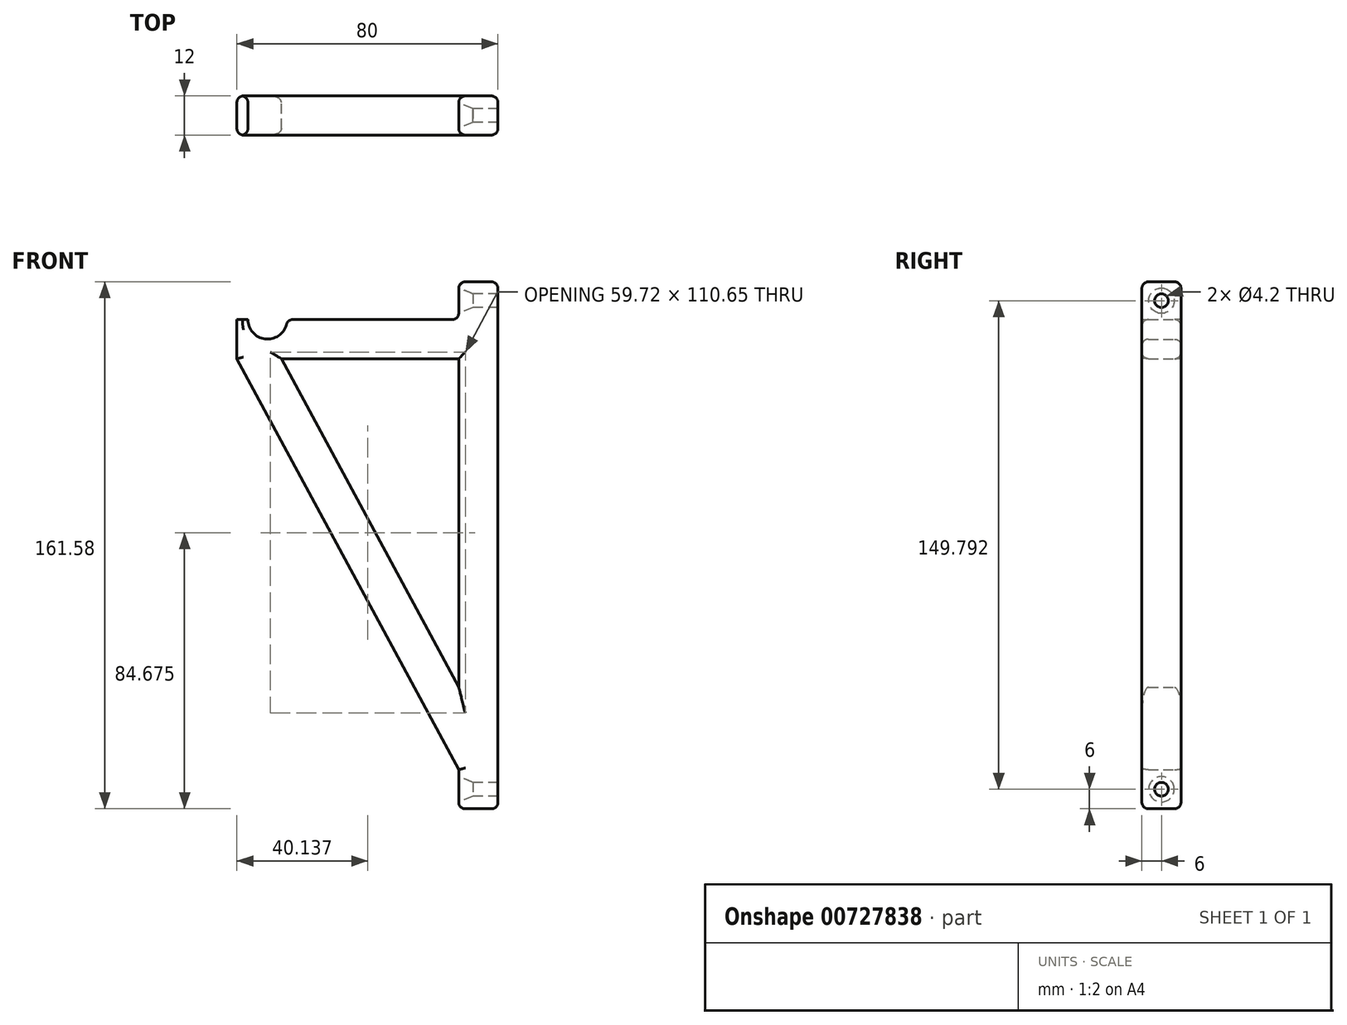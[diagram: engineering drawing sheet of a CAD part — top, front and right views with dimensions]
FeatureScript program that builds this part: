
annotation { "Feature Type Name" : "Feature", "Feature Type Description" : "" }
export const myFeature = defineFeature(function(context is Context, id is Id, definition is map)
    precondition{}
    {
        {
            var Q0;
            Q0=qCreatedBy(makeId("Front.planeOp"),FACE);
            var sketch = newSketch(context, id + "F0", { "sketchPlane" : qUnion([Q0])});
            skLineSegment(sketch, "E0", {"start": v(-21.3, 0) * mm, "end": v(46.7, 0) * mm});
            skLineSegment(sketch, "E1", {"start": v(46.7, 0) * mm, "end": v(46.7, -138) * mm});
            skLineSegment(sketch, "E2", {"start": v(46.7, -138) * mm, "end": v(58.7, -138) * mm});
            skLineSegment(sketch, "E3", {"start": v(58.7, -138) * mm, "end": v(58.7, -26.14) * mm});
            skLineSegment(sketch, "E4", {"start": v(58.7, -26.14) * mm, "end": v(58.7, 12) * mm});
            skLineSegment(sketch, "E5", {"start": v(58.7, 12) * mm, "end": v(-5.93, 12) * mm});
            skLineSegment(sketch, "E6", {"start": v(-21.3, 12) * mm, "end": v(-21.3, 0) * mm});
            skArc(sketch, "E7", {"start": v(-17.93, 12) * mm, "mid": v(-11.93, 6) * mm, "end": v(-5.93, 12) * mm});
            skLineSegment(sketch, "E8", {"start": v(58.7, 12) * mm, "end": v(58.7, 23.58) * mm});
            skLineSegment(sketch, "E9", {"start": v(58.7, 23.58) * mm, "end": v(46.7, 23.58) * mm});
            skLineSegment(sketch, "E10", {"start": v(46.7, 23.58) * mm, "end": v(46.7, 12) * mm});
            skLineSegment(sketch, "E11", {"start": v(-21.3, 0) * mm, "end": v(46.7, -126) * mm});
            skLineSegment(sketch, "E12", {"start": v(-7.66, 0) * mm, "end": v(46.7, -100.73) * mm});
            skLineSegment(sketch, "E13.trimOffspring", {"start": v(-17.93, 12) * mm, "end": v(-21.3, 12) * mm});
            skSolve(sketch);
        }
        {
            var Q0;
            {var subQ5=sQuery(id+"F0.wireOp",EDGE,"E2");Q0=makeQuery(id+"F0.imprint","IMPRINT",FACE,{"disambiguationData":[TD([[makeQuery(id+"F0.imprint","IMPRINT",EDGE,{"derivedFrom":subQ5}),1.0]])]});}
            var Q1;
            {var subQ0=sQuery(id+"F0.wireOp",EDGE,"MgnKtzhb-imRe-JAw6-ltcu-x3auhbO88FXf");Q1=makeQuery(id+"F0.imprint","IMPRINT",FACE,{"disambiguationData":[TD([[makeQuery(id+"F0.imprint","IMPRINT",EDGE,{"derivedFrom":subQ0}),1.0]])]});}
            var Q2;
            {var subQ0=sQuery(id+"F0.wireOp",EDGE,"E8");Q2=makeQuery(id+"F0.imprint","IMPRINT",FACE,{"disambiguationData":[TD([[makeQuery(id+"F0.imprint","IMPRINT",EDGE,{"derivedFrom":subQ0}),1.0]])]});}
            var Q3;
            {var subQ0=sQuery(id+"F0.wireOp",EDGE,"E11");Q3=makeQuery(id+"F0.imprint","IMPRINT",FACE,{"disambiguationData":[TD([[makeQuery(id+"F0.imprint","IMPRINT",EDGE,{"derivedFrom":subQ0}),1.0]])]});}
            extrude(context, id + "F1", {"entities" : qUnion([Q0, Q1, Q2, Q3]), "depth" : 12 * mm, "offsetDistance" : 25 * mm});
        }
        {
            var Q0;
            {var subQ0=sQuery(id+"F0.wireOp",EDGE,"E1");Q0=makeQuery(id+"F1.opExtrude","CAP_EDGE",EDGE,{"disambiguationData":[OSD([subQ0]),TDD([makeQuery(id+"F0.imprint","IMPRINT",EDGE,{"disambiguationData":[TD([[makeQuery(id+"F0.imprint","INTERSECT",VERTEX,{"derivedFrom":[subQ0,sQuery(id+"F0.wireOp",EDGE,"E2")]}),1.0]])],"derivedFrom":subQ0})])],"isStart":false});}
            var Q1;
            Q1=makeQuery(id+"F1.opExtrude","CAP_EDGE",EDGE,{"disambiguationData":[OSD([sQuery(id+"F0.wireOp",EDGE,"E5")])],"isStart":false});
            var Q2;
            Q2=makeQuery(id+"F1.opExtrude","CAP_EDGE",EDGE,{"disambiguationData":[OSD([sQuery(id+"F0.wireOp",EDGE,"E0")])],"isStart":false});
            var Q3;
            Q3=makeQuery(id+"F1.opExtrude","CAP_EDGE",EDGE,{"disambiguationData":[OSD([sQuery(id+"F0.wireOp",EDGE,"E6")])],"isStart":false});
            var Q4;
            Q4=makeQuery(id+"F1.opExtrude","CAP_EDGE",EDGE,{"disambiguationData":[OSD([sQuery(id+"F0.wireOp",EDGE,"E5")])],"isStart":true});
            var Q5;
            Q5=makeQuery(id+"F1.opExtrude","CAP_EDGE",EDGE,{"disambiguationData":[OSD([sQuery(id+"F0.wireOp",EDGE,"E3"),sQuery(id+"F0.wireOp",EDGE,"E4"),sQuery(id+"F0.wireOp",EDGE,"E8")])],"isStart":false});
            var Q6;
            Q6=makeQuery(id+"F1.opExtrude","SWEPT_EDGE",EDGE,{"disambiguationData":[OSD([sQuery(id+"F0.wireOp",EDGE,"E8"),sQuery(id+"F0.wireOp",EDGE,"E9")])]});
            var Q7;
            Q7=makeQuery(id+"F1.opExtrude","SWEPT_EDGE",EDGE,{"disambiguationData":[OSD([sQuery(id+"F0.wireOp",EDGE,"E2"),sQuery(id+"F0.wireOp",EDGE,"E3")])]});
            var Q8;
            Q8=makeQuery(id+"F1.opExtrude","SWEPT_EDGE",EDGE,{"disambiguationData":[OSD([sQuery(id+"F0.wireOp",EDGE,"E5"),sQuery(id+"F0.wireOp",EDGE,"E7")])]});
            var Q9;
            Q9=makeQuery(id+"F1.opExtrude","SWEPT_EDGE",EDGE,{"disambiguationData":[OSD([sQuery(id+"F0.wireOp",EDGE,"E5"),sQuery(id+"F0.wireOp",EDGE,"E10")])]});
            var Q10;
            Q10=makeQuery(id+"F1.opExtrude","CAP_EDGE",EDGE,{"disambiguationData":[OSD([sQuery(id+"F0.wireOp",EDGE,"E3"),sQuery(id+"F0.wireOp",EDGE,"E4"),sQuery(id+"F0.wireOp",EDGE,"E8")])],"isStart":true});
            var Q11;
            Q11=makeQuery(id+"F1.opExtrude","CAP_EDGE",EDGE,{"disambiguationData":[OSD([sQuery(id+"F0.wireOp",EDGE,"E2")])],"isStart":true});
            var Q12;
            Q12=makeQuery(id+"F1.opExtrude","CAP_EDGE",EDGE,{"disambiguationData":[OSD([sQuery(id+"F0.wireOp",EDGE,"E2")])],"isStart":false});
            var Q13;
            Q13=makeQuery(id+"F1.opExtrude","CAP_EDGE",EDGE,{"disambiguationData":[OSD([sQuery(id+"F0.wireOp",EDGE,"E10")])],"isStart":true});
            var Q14;
            Q14=makeQuery(id+"F1.opExtrude","CAP_EDGE",EDGE,{"disambiguationData":[OSD([sQuery(id+"F0.wireOp",EDGE,"E9")])],"isStart":true});
            var Q15;
            Q15=makeQuery(id+"F1.opExtrude","CAP_EDGE",EDGE,{"disambiguationData":[OSD([sQuery(id+"F0.wireOp",EDGE,"E6")])],"isStart":true});
            var Q16;
            Q16=makeQuery(id+"F1.opExtrude","CAP_EDGE",EDGE,{"disambiguationData":[OSD([sQuery(id+"F0.wireOp",EDGE,"E9")])],"isStart":false});
            var Q17;
            Q17=makeQuery(id+"F1.opExtrude","SWEPT_EDGE",EDGE,{"disambiguationData":[OSD([sQuery(id+"F0.wireOp",EDGE,"E9"),sQuery(id+"F0.wireOp",EDGE,"E10")])]});
            var Q18;
            Q18=makeQuery(id+"F1.opExtrude","CAP_EDGE",EDGE,{"disambiguationData":[OSD([sQuery(id+"F0.wireOp",EDGE,"E10")])],"isStart":false});
            var Q19;
            {var subQ0=sQuery(id+"F0.wireOp",EDGE,"E1");Q19=makeQuery(id+"F1.opExtrude","CAP_EDGE",EDGE,{"disambiguationData":[OSD([subQ0]),TDD([makeQuery(id+"F0.imprint","IMPRINT",EDGE,{"disambiguationData":[TD([[makeQuery(id+"F0.imprint","INTERSECT",VERTEX,{"derivedFrom":[subQ0,sQuery(id+"F0.wireOp",EDGE,"E2")]}),1.0]])],"derivedFrom":subQ0})])],"isStart":true});}
            var Q20;
            Q20=makeQuery(id+"F1.opExtrude","SWEPT_EDGE",EDGE,{"disambiguationData":[OSD([sQuery(id+"F0.wireOp",EDGE,"E1"),sQuery(id+"F0.wireOp",EDGE,"E2")])]});
            var Q21;
            Q21=makeQuery(id+"F1.opExtrude","CAP_EDGE",EDGE,{"disambiguationData":[OSD([sQuery(id+"F0.wireOp",EDGE,"E11")])],"isStart":false});
            var Q22;
            Q22=makeQuery(id+"F1.opExtrude","CAP_EDGE",EDGE,{"disambiguationData":[OSD([sQuery(id+"F0.wireOp",EDGE,"E11")])],"isStart":true});
            var Q23;
            Q23=makeQuery(id+"F1.opExtrude","CAP_FACE",FACE,{"disambiguationData":[OSD([sQuery(id+"F0.wireOp",EDGE,"E0"),sQuery(id+"F0.wireOp",EDGE,"E1"),sQuery(id+"F0.wireOp",EDGE,"E2"),sQuery(id+"F0.wireOp",EDGE,"E3"),sQuery(id+"F0.wireOp",EDGE,"E4"),sQuery(id+"F0.wireOp",EDGE,"E5"),sQuery(id+"F0.wireOp",EDGE,"E6"),sQuery(id+"F0.wireOp",EDGE,"E7"),sQuery(id+"F0.wireOp",EDGE,"E8"),sQuery(id+"F0.wireOp",EDGE,"E9"),sQuery(id+"F0.wireOp",EDGE,"E10"),sQuery(id+"F0.wireOp",EDGE,"E11"),sQuery(id+"F0.wireOp",EDGE,"E12"),sQuery(id+"F0.wireOp",EDGE,"E13.trimOffspring")])],"isStart":false});
            var Q24;
            {var subQ0=sQuery(id+"F0.wireOp",EDGE,"E1");Q24=makeQuery(id+"F1.opExtrude","CAP_EDGE",EDGE,{"disambiguationData":[OSD([subQ0]),TDD([makeQuery(id+"F0.imprint","IMPRINT",EDGE,{"disambiguationData":[TD([[makeQuery(id+"F0.imprint","INTERSECT",VERTEX,{"derivedFrom":[sQuery(id+"F0.wireOp",EDGE,"E0"),subQ0]}),-1.0]])],"derivedFrom":subQ0})])],"isStart":true});}
            var Q25;
            Q25=makeQuery(id+"F1.opExtrude","CAP_EDGE",EDGE,{"disambiguationData":[OSD([sQuery(id+"F0.wireOp",EDGE,"E12")])],"isStart":true});
            var Q26;
            Q26=makeQuery(id+"F1.opExtrude","CAP_EDGE",EDGE,{"disambiguationData":[OSD([sQuery(id+"F0.wireOp",EDGE,"E12")])],"isStart":false});
            var Q27;
            Q27=makeQuery(id+"F1.opExtrude","CAP_EDGE",EDGE,{"disambiguationData":[OSD([sQuery(id+"F0.wireOp",EDGE,"E0")])],"isStart":true});
            var Q28;
            Q28=makeQuery(id+"F1.opExtrude","CAP_EDGE",EDGE,{"disambiguationData":[OSD([sQuery(id+"F0.wireOp",EDGE,"E7")])],"isStart":true});
            fillet(context, id + "F2", {"entities" : qUnion([Q0, Q1, Q2, Q3, Q4, Q5, Q6, Q7, Q8, Q9, Q10, Q11, Q12, Q13, Q14, Q15, Q16, Q17, Q18, Q19, Q20, Q21, Q22, Q23, Q24, Q25, Q26, Q27, Q28]), "radius" : 2 * mm, "tangentPropagation" : true, "allowEdgeOverflow" : false});
        }
        {
            var Q0;
            Q0=makeQuery(id+"F1.opExtrude","SWEPT_FACE",FACE,{"disambiguationData":[OSD([sQuery(id+"F0.wireOp",EDGE,"E10")])]});
            var sketch = newSketch(context, id + "F3", { "sketchPlane" : qUnion([Q0])});
            skLineSegment(sketch, "E14", {"start": v(2, 21.58) * mm, "end": v(10, 14) * mm, "construction": true});
            skLineSegment(sketch, "E15", {"start": v(2, 14) * mm, "end": v(10, 21.58) * mm, "construction": true});
            skCircle(sketch, "E16", {"center": v(6, 17.8) * mm, "radius": 2.36 * mm});
            skLineSegment(sketch, "E17", {"start": v(2.2, -126.31) * mm, "end": v(9.99, -137.98) * mm, "construction": true});
            skLineSegment(sketch, "E18", {"start": v(9.99, -125.98) * mm, "end": v(2.2, -137.75) * mm, "construction": true});
            skCircle(sketch, "E19", {"center": v(6, -132) * mm, "radius": 3.9 * mm});
            skSolve(sketch);
        }
        {
            var Q0;
            Q0=sQuery(id+"F3.wireOp",VERTEX,"E16.center");
            var Q1;
            Q1=makeQuery(id+"F1.opExtrude","SWEPT_BODY",BODY,{"disambiguationData":[OSD([sQuery(id+"F0.wireOp",EDGE,"E0"),sQuery(id+"F0.wireOp",EDGE,"E1"),sQuery(id+"F0.wireOp",EDGE,"E2"),sQuery(id+"F0.wireOp",EDGE,"E3"),sQuery(id+"F0.wireOp",EDGE,"E4"),sQuery(id+"F0.wireOp",EDGE,"E5"),sQuery(id+"F0.wireOp",EDGE,"E6"),sQuery(id+"F0.wireOp",EDGE,"E7"),sQuery(id+"F0.wireOp",EDGE,"E8"),sQuery(id+"F0.wireOp",EDGE,"E9"),sQuery(id+"F0.wireOp",EDGE,"E10"),sQuery(id+"F0.wireOp",EDGE,"E11"),sQuery(id+"F0.wireOp",EDGE,"E12"),sQuery(id+"F0.wireOp",EDGE,"E13.trimOffspring")])]});
            hole(context, id + "F4", {"style" : HoleStyle.C_SINK, "endStyle" : HoleEndStyle.THROUGH, "holeDiameter" : 4.2 * mm, "cSinkDiameter" : 7.8 * mm, "cSinkAngle" : 45 * degree, "majorDiameter" : 5 * mm, "isTappedThrough" : true, "tappedDepth" : 12 * mm, "tapClearance" : 3, "startFromSketch" : true, "locations" : qUnion([Q0]), "scope" : qUnion([Q1])});
        }
        {
            var Q0;
            {var subQ0=sQuery(id+"F0.wireOp",EDGE,"E1");Q0=makeQuery(id+"F1.opExtrude","SWEPT_FACE",FACE,{"disambiguationData":[OSD([subQ0]),TDD([makeQuery(id+"F0.imprint","IMPRINT",EDGE,{"disambiguationData":[TD([[makeQuery(id+"F0.imprint","INTERSECT",VERTEX,{"derivedFrom":[subQ0,sQuery(id+"F0.wireOp",EDGE,"E2")]}),1.0]])],"derivedFrom":subQ0})])]});}
            var sketch = newSketch(context, id + "F5", { "sketchPlane" : qUnion([Q0])});
            skLineSegment(sketch, "E20", {"start": v(2, -126) * mm, "end": v(10, -138) * mm, "construction": true});
            skLineSegment(sketch, "E21", {"start": v(10, -126) * mm, "end": v(2, -138) * mm, "construction": true});
            skCircle(sketch, "E22", {"center": v(6, -132) * mm, "radius": 3.86 * mm});
            skSolve(sketch);
        }
        {
            var Q0;
            Q0=sQuery(id+"F5.wireOp",VERTEX,"E22.center");
            var Q1;
            Q1=makeQuery(id+"F1.opExtrude","SWEPT_BODY",BODY,{"disambiguationData":[OSD([sQuery(id+"F0.wireOp",EDGE,"E0"),sQuery(id+"F0.wireOp",EDGE,"E1"),sQuery(id+"F0.wireOp",EDGE,"E2"),sQuery(id+"F0.wireOp",EDGE,"E3"),sQuery(id+"F0.wireOp",EDGE,"E4"),sQuery(id+"F0.wireOp",EDGE,"E5"),sQuery(id+"F0.wireOp",EDGE,"E6"),sQuery(id+"F0.wireOp",EDGE,"E7"),sQuery(id+"F0.wireOp",EDGE,"E8"),sQuery(id+"F0.wireOp",EDGE,"E9"),sQuery(id+"F0.wireOp",EDGE,"E10"),sQuery(id+"F0.wireOp",EDGE,"E11"),sQuery(id+"F0.wireOp",EDGE,"E12"),sQuery(id+"F0.wireOp",EDGE,"E13.trimOffspring")])]});
            hole(context, id + "F6", {"style" : HoleStyle.C_SINK, "endStyle" : HoleEndStyle.THROUGH, "holeDiameter" : 4.2 * mm, "cSinkDiameter" : 7.8 * mm, "cSinkAngle" : 45 * degree, "majorDiameter" : 5 * mm, "isTappedThrough" : true, "tappedDepth" : 12 * mm, "tapClearance" : 3, "startFromSketch" : true, "locations" : qUnion([Q0]), "scope" : qUnion([Q1])});
        }
    });
